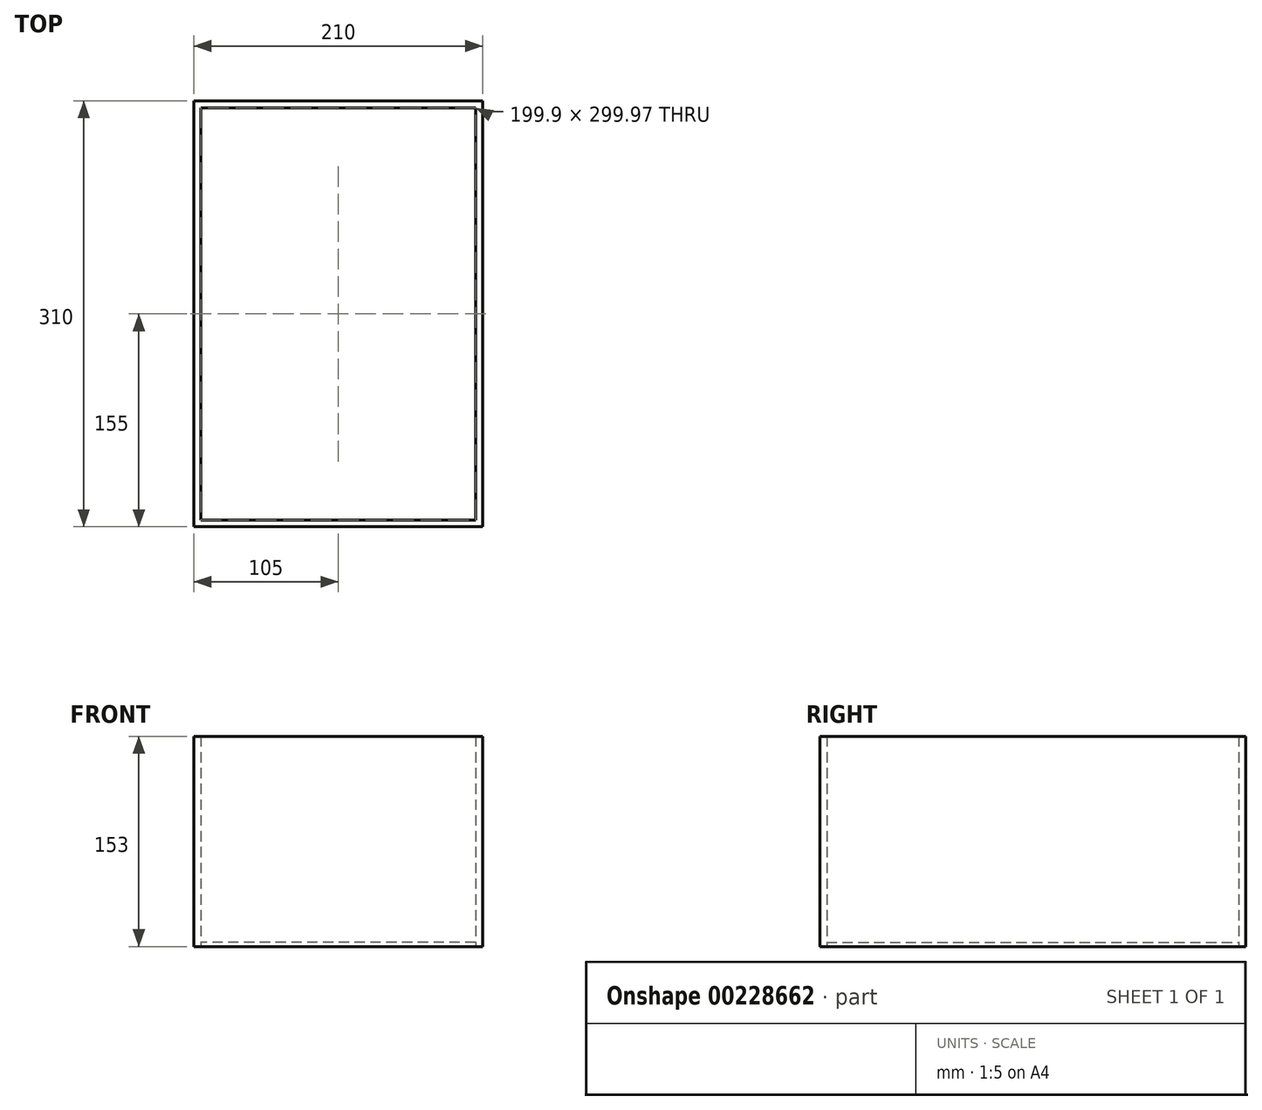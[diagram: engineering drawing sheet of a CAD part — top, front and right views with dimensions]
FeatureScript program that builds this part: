
annotation { "Feature Type Name" : "Feature", "Feature Type Description" : "" }
export const myFeature = defineFeature(function(context is Context, id is Id, definition is map)
    precondition{}
    {
        {
            var Q0;
            Q0=qCreatedBy(makeId("Top.planeOp"),FACE);
            var sketch = newSketch(context, id + "F0", { "sketchPlane" : qUnion([Q0])});
            skLineSegment(sketch, "E0.bottom", {"start": v(99.95, -149.99) * mm, "end": v(-99.95, -149.99) * mm});
            skLineSegment(sketch, "E0.top", {"start": v(99.95, 149.99) * mm, "end": v(-99.95, 149.99) * mm});
            skLineSegment(sketch, "E0.left", {"start": v(99.95, -149.99) * mm, "end": v(99.95, 149.99) * mm});
            skLineSegment(sketch, "E0.right", {"start": v(-99.95, -149.99) * mm, "end": v(-99.95, 149.99) * mm});
            skPoint(sketch, "E0.middle", {"position": v(0, 0) * mm});
            skLineSegment(sketch, "E1.bottom", {"start": v(105, -155) * mm, "end": v(-105, -155) * mm});
            skLineSegment(sketch, "E1.top", {"start": v(105, 155) * mm, "end": v(-105, 155) * mm});
            skLineSegment(sketch, "E1.left", {"start": v(105, -155) * mm, "end": v(105, 155) * mm});
            skLineSegment(sketch, "E1.right", {"start": v(-105, -155) * mm, "end": v(-105, 155) * mm});
            skSolve(sketch);
        }
        {
            var Q0;
            Q0 = qSketchRegion(id + "F0", true);
            extrude(context, id + "F1", {"entities" : qUnion([Q0]), "depth" : 153 * mm});
        }
        {
            var Q0;
            Q0=makeQuery(id+"F0.imprint","IMPRINT",FACE,{"disambiguationData":[TD([[makeQuery(id+"F0.imprint","IMPRINT",EDGE,{"derivedFrom":sQuery(id+"F0.wireOp",EDGE,"E0.bottom")}),-1.0]])]});
            extrude(context, id + "F2", {"entities" : qUnion([Q0]), "depth" : 3 * mm});
        }
    });
